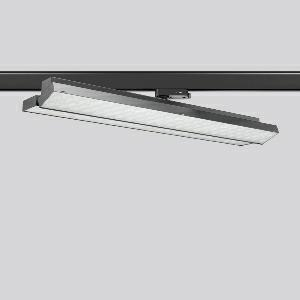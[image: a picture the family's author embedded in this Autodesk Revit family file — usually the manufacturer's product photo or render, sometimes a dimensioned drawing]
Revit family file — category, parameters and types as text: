
# Revit family: tx-move_742163_003_76_1b08
name_source: partatom
category: Lighting Fixtures
units: mm (PartAtom-declared; Revit-internal decimal feet)

## family parameters
Cut with Voids When Loaded = No
Host = Face
Light Source = No
Part Type = Normal
Room Calculation Point = No
Round Connector Dimension = Use Diameter
Shared = No

## types (1)
- MultiLumen 1 (1 x LED Modul 830, 2750 lm, 3000)
    Apparent Load = 41 VA
    CIE Flux Codes = 65 90 98 100 100
    Color Rendering = 80
    Color Temperature = 3000
    Default Elevation = 1800 mm
    Description = Series: TX-MOVE
Multifunctional surface-mounted spotlight for area lighting. Very flat design. Housing: sheet steel, powder-coated. Rotation range: 356°. Swivel range: 90°. Consistent alignment possible with visible tilt scale. High-efficiency LED units with optimum light control thanks to clear plastic (PC) lens optics. Spezielle Mikrostrukturen reduzieren Gelbsaum. Asymmetrical light distribution. With adapter for RZB 3-circuit DALI tracks. Suitable for Track on ceiling. MultiLumen: Luminous flux adjustable in 3 steps. Factory setting is the highest luminous flux. Environmentally friendly and resource-saving due to replaceable and recyclable components. 
Colour: deep black, matt (RAL 9005)
Length: 570 mm
Width: 119 mm
Height: 88 mm
Lamp: LED
Socket: without socket
Colour temperature: 3000K
Colour rendering index (CRI): 80
System power: 41 W
Rated luminous flux: 5500 lm
Luminous efficiency: 134 lm/W
System power 2: 57 W
Rated luminous flux 2: 7400 lm
Luminous efficiency 2: 130 lm/W
System power 3: 73 W
Rated luminous flux 3: 9050 lm
Luminous efficiency 3: 124 lm/W
Control gear: Dimmable EVG, DALI
Protection class: I
Type of protection: IP 20
    Height = 75 mm
    Lamp = 1 x LED Modul 830
    Lamp Light Flux = 2750 lm
    Lamp count = 1
    Length = 569 mm
    Lifetime = 50000 h
    Luminous efficacy = 134 lm/W
    Manufacturer = RZB
    ModVariant = No
    Model = 742163.003.76
    Mounting Place = Ceiling
    Mounting Type = Surface mounted
    Number of Poles = 1
    OnlyDefault = Yes
    Power Factor = 1
    Product Name = TX-MOVE
    Product group = Track mounted projectors
    ProductGroupID = 301
    Protection Class = Protection class I
    Protection Degree = IP 20
    RLX_Detail_Level = 1
    RLX_Emergency_Light_Flux = 0 lm
    RLX_Emergency_Type = 0
    RLX_Emergency_Type_DB = No
    RlxData = <blob elided: 57485 chars, md5=53183a73>
    Socket = socket
    Standby Power = 0 W
    System Light Flux = 5500 lm
    System Power = 41 W
    Type Comments = MultiLumen 1
    Type Image = 742162.003.jpg
    URL = http://relux.com
    VarID = multilumen_1
    Voltage = 0 V
    Weight = 0.00 kg
    Width = 119 mm

## geometry (parser evidence)
native form markers: Blend x4, Sweep x17
no freeform markers — native parametric forms only
